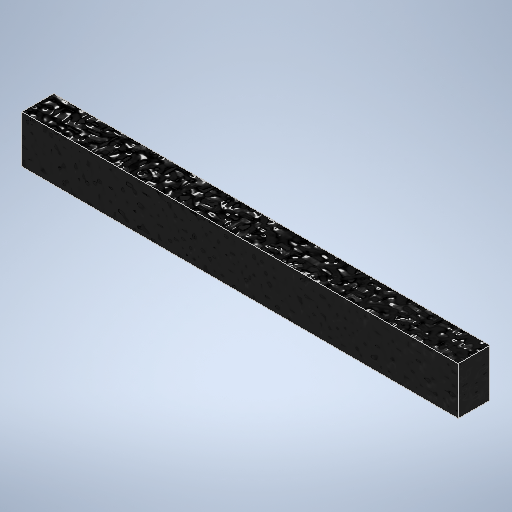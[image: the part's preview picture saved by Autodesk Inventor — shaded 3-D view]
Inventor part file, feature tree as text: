
AUTODESK INVENTOR PART (.ipt)
format: ipt  version: 2025 (Build 290162010, 162A)  size: 424,448 bytes
history: native  units: in
note: dims shown in document units (in); Inventor stores cm internally (conversion verified against a paired STEP export)
features: extrude x1, sketch x1
ambient origin geometry x8: Origin, YZ Plane, XZ Plane, XY Plane, X Axis, Y Axis, Z Axis, Center Point
bodies: Solid1 (feature_tree)
feature tree (2):
  extrude  "Extrusion1"  Depth=13.75in
  sketch  "Sketch1"  dims[d2=1.5in d3=13.75in d4=1.0in d5=0.0in]
